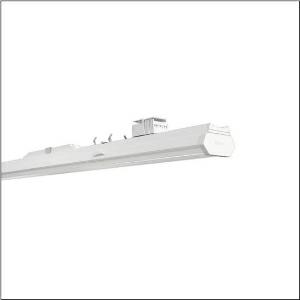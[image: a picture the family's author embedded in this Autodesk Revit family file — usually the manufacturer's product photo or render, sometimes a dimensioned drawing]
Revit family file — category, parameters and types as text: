
# Revit family: licross_r__21_protected_mo_52td1bvn45xgd_2e06
name_source: partatom
category: Lighting Fixtures
units: mm (PartAtom-declared; Revit-internal decimal feet)

## family parameters
Cut with Voids When Loaded = No
Host = Face
Light Source = No
Part Type = Normal
Room Calculation Point = No
Round Connector Dimension = Use Diameter
Shared = No

## types (1)
- --- (1 x LED, 5000 lm, 29.3 W, 4000K)
    Apparent Load = 29 VA
    CIE Flux Codes = 54 82 95 97 100
    Color Rendering = 80
    Color Temperature = 4000K
    Default Elevation = 1800 mm
    Description = Licross® 21 Protected MO, luminaire insert, of sheet steel, galvanised, coil coated, white, length: 1.500mm, width: 90mm, height: 101mm, LED rated luminous flux: 5.000lm, light colour: 840, control gear: DALI 2, CLO (for two DALI lines), with plug, 6-pole, with phase selection, mains connection: 220..240V, AC/DC, 0/50..60Hz, start of lifetime: 29W, end of service life: 33W, halogen-free wiring, for central battery installations according to DIN EN 60598-2-22, for emergency light function, without changeover relay, primary optical cover: cover, of PMMA, light emission: direct distribution, primary light characteristic: symmetric, protection rating (complete): IP54, insulation class (complete): insulation class I (protective earthing), certification: CE, ENEC, VDE, UKCA, protection symbol: D if used in an environment with non-conductive dust loads with corresponding accessories, impact resistance: IK06, permissible ambient temperature for indoor applications: -25..+50°C, standard: EN 60598-2-22, corresponds to IFS (International Featured Standards) requirements for safety and quality in the food industry, reducing of maximum allowable ambient temperature of 5°C with ceiling mounting, LABS conformity tested according to VDMA 24364:2018-05, packaging unit: 1 piece
    Height = 92 mm
    Lamp = 1 x LED
    Lamp Light Flux = 5000 lm
    Lamp Power = 29.3 W
    Lamp count = 1
    Length = 1500 mm
    Luminous efficacy = 171 lm/W
    Manufacturer = Siteco
    ModVariant = No
    Model = 52TD1BVN45XGD
    Mounting Place = Ceiling
    Mounting Type = Pendant
    Number of Poles = 1
    OnlyDefault = Yes
    Power Factor = 1
    Product Name = Licross® 21 Protected MO
    Product group = luminaire insert
    ProductGroupID = 902
    Protection Class = Protection class I
    Protection Degree = IP 54
    RLX_Detail_Level = 1
    RLX_Emergency_Light_Flux = 0 lm
    RLX_Emergency_Type = 0
    RLX_Emergency_Type_DB = No
    RlxData = <blob elided: 24321 chars, md5=92aa1ba6>
    Socket = socket
    Standby Power = 0 W
    System Light Flux = 5000 lm
    System Power = 29 W
    Type Comments = : AC-mode, luminous flux: 100 % | dim-lin: 254 | 199 mA
    Type Image = l_1256148.jpg
    URL = http://relux.com
    VarID = @adj_102360
    Voltage = 0 V
    Weight = 0.00 kg
    Width = 88 mm

## geometry (parser evidence)
native form markers: Blend x4, Sweep x9
no freeform markers — native parametric forms only
